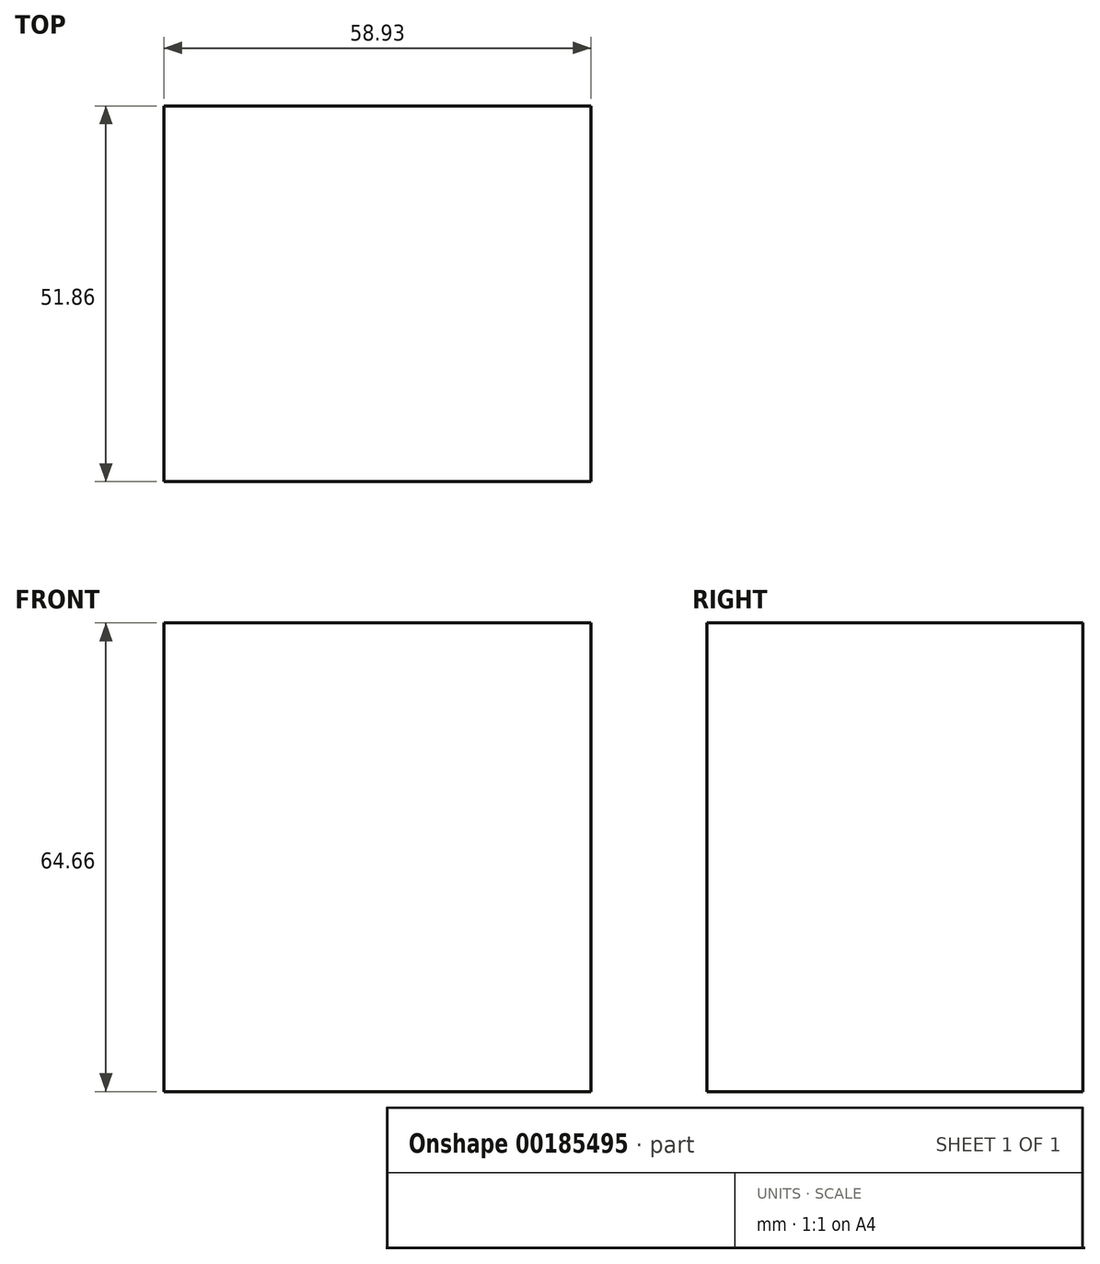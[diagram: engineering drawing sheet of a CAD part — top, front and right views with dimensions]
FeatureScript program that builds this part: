
annotation { "Feature Type Name" : "Feature", "Feature Type Description" : "" }
export const myFeature = defineFeature(function(context is Context, id is Id, definition is map)
    precondition{}
    {
        {
            var Q0;
            Q0=qCreatedBy(makeId("Right.planeOp"),FACE);
            var sketch = newSketch(context, id + "F0", { "sketchPlane" : qUnion([Q0])});
            skLineSegment(sketch, "E0.bottom", {"start": v(-41.87, 38.74) * mm, "end": v(9.99, 38.74) * mm});
            skLineSegment(sketch, "E0.top", {"start": v(-41.87, -25.92) * mm, "end": v(9.99, -25.92) * mm});
            skLineSegment(sketch, "E0.left", {"start": v(-41.87, 38.74) * mm, "end": v(-41.87, -25.92) * mm});
            skLineSegment(sketch, "E0.right", {"start": v(9.99, 38.74) * mm, "end": v(9.99, -25.92) * mm});
            skSolve(sketch);
        }
        {
            var Q0;
            Q0=makeQuery(id+"F0.imprint","IMPRINT",FACE,{"disambiguationData":[TD([[makeQuery(id+"F0.imprint","IMPRINT",EDGE,{"derivedFrom":sQuery(id+"F0.wireOp",EDGE,"E0.bottom")}),-1.0]])]});
            extrude(context, id + "F1", {"entities" : qUnion([Q0]), "depth" : 58.93 * mm});
        }
    });
